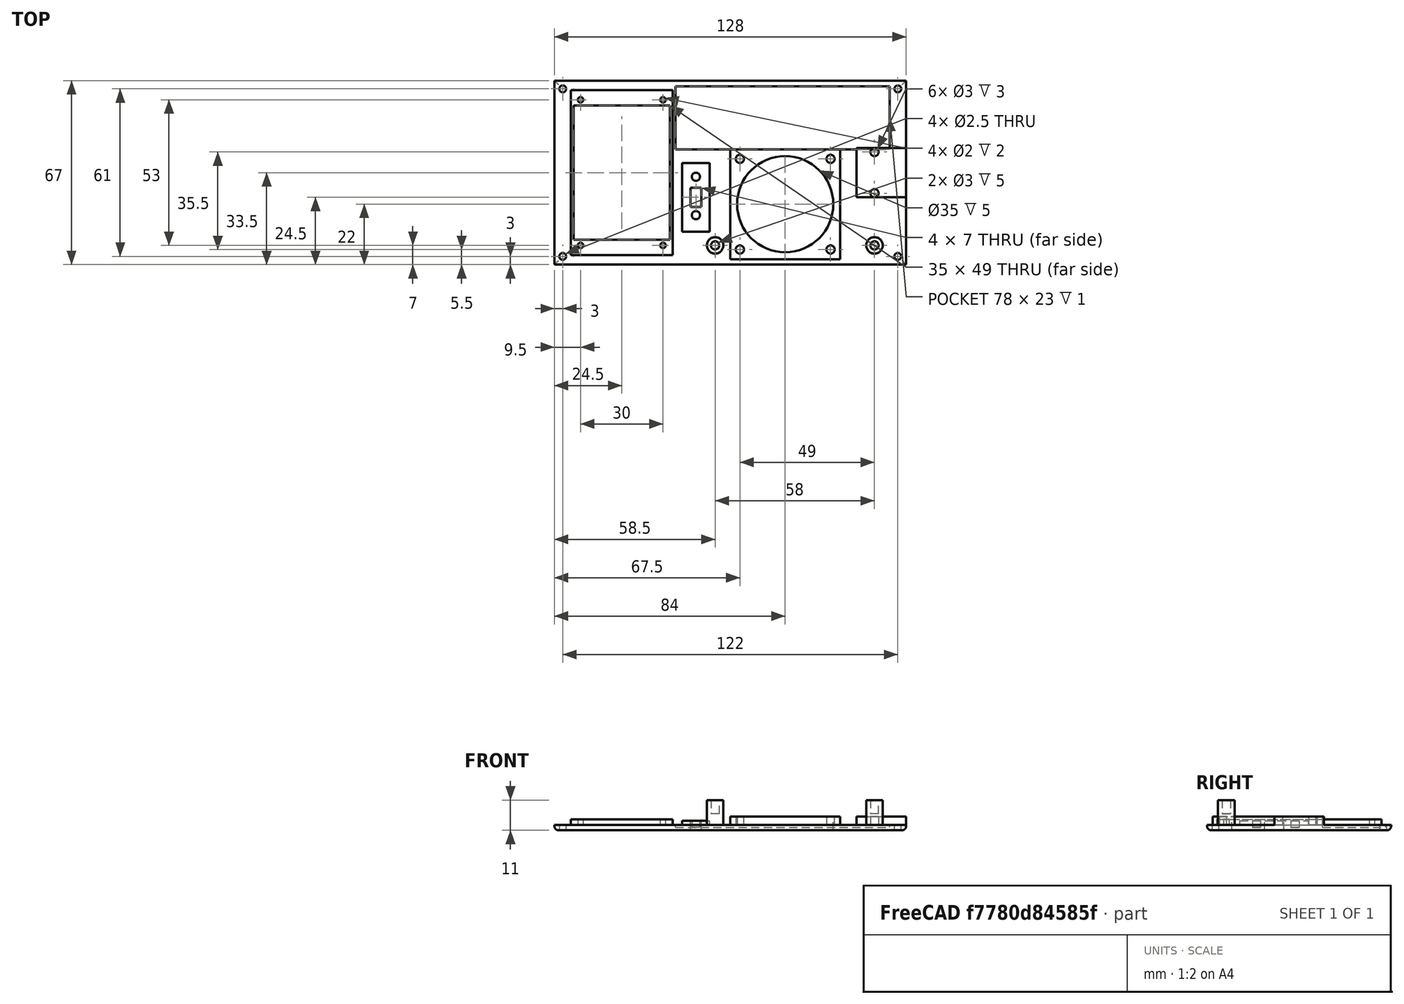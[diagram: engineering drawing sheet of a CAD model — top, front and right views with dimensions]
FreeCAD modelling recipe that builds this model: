
FCSTD DOCUMENT  (FreeCAD 1.0R39319 (Git))
Label: caseTopRedesign
License: All rights reserved
LicenseURL: https://en.wikipedia.org/wiki/All_rights_reserved
objects: PartDesign::SubtractiveCylinder×19, PartDesign::AdditiveBox×5, PartDesign::SubtractiveBox×3, PartDesign::AdditiveCylinder×2, PartDesign::Fillet×1, PartDesign::Body×1
note: 91 computed .brp shape members not serialized (recipe doc carries the construction recipe); baked Part::Feature solids carry a one-line shape summary decoded from their .brp

FEATURE [PartDesign::AdditiveBox] Box  label="base"
  AttacherType = Attacher::AttachEngine3D
  Height = 2
  Length = 128
  Refine = true
  Suppressed = false
  Width = 67
FEATURE [PartDesign::AdditiveBox] Box001  label="screenBase"
  AttacherType = Attacher::AttachEngine3D
  AttachmentOffset = pos=(6,3.5,0) rot=(0,0,1;0rad)
  AttachmentSupport = -> [Box]
  BaseFeature = -> Box
  Height = 2
  Length = 37
  MapMode = 5
  Placement = pos=(6,3.5,2) rot=(0,0,1;0rad)
  Refine = true
  Suppressed = false
  Width = 60
FEATURE [PartDesign::SubtractiveBox] Box002  label="screenCutout"
  AttacherType = Attacher::AttachEngine3D
  AttachmentOffset = pos=(1,5.5,-4) rot=(0,0,1;0rad)
  AttachmentSupport = -> [Box001]
  BaseFeature = -> Box001
  Height = 4
  Length = 35
  MapMode = 5
  Placement = pos=(7,9,0) rot=(0,0,1;0rad)
  Refine = true
  Suppressed = false
  Width = 49
FEATURE [PartDesign::SubtractiveBox] Box003  label="batteryRecess"
  AttacherType = Attacher::AttachEngine3D
  AttachmentOffset = pos=(37,33,-1) rot=(0,0,1;0rad)
  AttachmentSupport = -> [Box002]
  BaseFeature = -> Box002
  Height = 1
  Length = 78
  MapMode = 5
  Placement = pos=(44,42,1) rot=(0,0,1;0rad)
  Refine = true
  Suppressed = false
  Width = 23
FEATURE [PartDesign::AdditiveBox] Box004  label="clickwheelBase"
  AttacherType = Attacher::AttachEngine3D
  AttachmentOffset = pos=(20,-40,0) rot=(0,0,1;0rad)
  AttachmentSupport = -> [Box003]
  BaseFeature = -> Box003
  Height = 3
  Length = 40
  MapMode = 5
  Placement = pos=(64,2,2) rot=(0,0,1;0rad)
  Refine = true
  Suppressed = false
  Width = 40
FEATURE [PartDesign::SubtractiveCylinder] Cylinder  label="clickwheelCutout"
  Angle = 360
  AttacherType = Attacher::AttachEngine3D
  AttachmentOffset = pos=(20,20,-5) rot=(0,0,1;0rad)
  AttachmentSupport = -> [Box004]
  BaseFeature = -> Box004
  FirstAngle = 0
  Height = 5
  MapMode = 5
  Placement = pos=(84,22,0) rot=(0,0,1;0rad)
  Radius = 17.5
  Refine = true
  SecondAngle = 0
  Suppressed = false
FEATURE [PartDesign::SubtractiveCylinder] Cylinder001  label="clickwheelTopLeftScrew"
  Angle = 360
  AttacherType = Attacher::AttachEngine3D
  AttachmentOffset = pos=(-16.5,-16.5,-3) rot=(0,0,1;0rad)
  AttachmentSupport = -> [Cylinder]
  BaseFeature = -> Cylinder
  FirstAngle = 0
  Height = 3
  MapMode = 5
  Placement = pos=(67.5,5.5,2) rot=(0,0,1;0rad)
  Radius = 1.5
  Refine = true
  SecondAngle = 0
  Suppressed = false
FEATURE [PartDesign::SubtractiveCylinder] Cylinder002  label="clickwheelTopRightScrew"
  Angle = 360
  AttacherType = Attacher::AttachEngine3D
  AttachmentOffset = pos=(0,33,-3) rot=(0,0,1;0rad)
  AttachmentSupport = -> [Cylinder001]
  BaseFeature = -> Cylinder001
  FirstAngle = 0
  Height = 3
  MapMode = 5
  Placement = pos=(67.5,38.5,2) rot=(0,0,1;0rad)
  Radius = 1.5
  Refine = true
  SecondAngle = 0
  Suppressed = false
FEATURE [PartDesign::SubtractiveCylinder] Cylinder003  label="clickwheelBottomRightScrew"
  Angle = 360
  AttacherType = Attacher::AttachEngine3D
  AttachmentOffset = pos=(33,0,-3) rot=(0,0,1;0rad)
  AttachmentSupport = -> [Cylinder002]
  BaseFeature = -> Cylinder002
  FirstAngle = 0
  Height = 3
  MapMode = 5
  Placement = pos=(100.5,38.5,2) rot=(0,0,1;0rad)
  Radius = 1.5
  Refine = true
  SecondAngle = 0
  Suppressed = false
FEATURE [PartDesign::SubtractiveCylinder] Cylinder004  label="clickwheelBottomLeftScrew"
  Angle = 360
  AttacherType = Attacher::AttachEngine3D
  AttachmentOffset = pos=(0,-33,-3) rot=(0,0,1;0rad)
  AttachmentSupport = -> [Cylinder003]
  BaseFeature = -> Cylinder003
  FirstAngle = 0
  Height = 3
  MapMode = 5
  Placement = pos=(100.5,5.5,2) rot=(0,0,1;0rad)
  Radius = 1.5
  Refine = true
  SecondAngle = 0
  Suppressed = false
FEATURE [PartDesign::AdditiveBox] Box005  label="chargingBase"
  AttacherType = Attacher::AttachEngine3D
  AttachmentOffset = pos=(9.5,19,0) rot=(0,0,1;0rad)
  AttachmentSupport = -> [Cylinder004]
  BaseFeature = -> Cylinder004
  Height = 3
  Length = 18
  MapMode = 5
  Placement = pos=(110,24.5,2) rot=(0,0,1;0rad)
  Refine = true
  Suppressed = false
  Width = 18
FEATURE [PartDesign::SubtractiveCylinder] Cylinder005  label="chargingScrewLeft"
  Angle = 360
  AttacherType = Attacher::AttachEngine3D
  AttachmentOffset = pos=(6.5,1.5,-3) rot=(0,0,1;0rad)
  AttachmentSupport = -> [Box005]
  BaseFeature = -> Box005
  FirstAngle = 0
  Height = 3
  MapMode = 5
  Placement = pos=(116.5,26,2) rot=(0,0,1;0rad)
  Radius = 1.5
  Refine = true
  SecondAngle = 0
  Suppressed = false
FEATURE [PartDesign::SubtractiveCylinder] Cylinder006  label="chargingScrewRight"
  Angle = 360
  AttacherType = Attacher::AttachEngine3D
  AttachmentOffset = pos=(0,15,-3) rot=(0,0,1;0rad)
  AttachmentSupport = -> [Cylinder005]
  BaseFeature = -> Cylinder005
  FirstAngle = 0
  Height = 3
  MapMode = 5
  Placement = pos=(116.5,41,2) rot=(0,0,1;0rad)
  Radius = 1.5
  Refine = true
  SecondAngle = 0
  Suppressed = false
FEATURE [PartDesign::AdditiveCylinder] Cylinder007
  Angle = 360
  AttacherType = Attacher::AttachEngine3D
  AttachmentOffset = pos=(0,-34,0) rot=(0,0,1;0rad)
  AttachmentSupport = -> [Cylinder006]
  BaseFeature = -> Cylinder006
  FirstAngle = 0
  Height = 9
  MapMode = 5
  Placement = pos=(116.5,7,2) rot=(0,0,1;0rad)
  Radius = 3
  Refine = true
  SecondAngle = 0
  Suppressed = false
FEATURE [PartDesign::SubtractiveCylinder] Cylinder008
  Angle = 360
  AttacherType = Attacher::AttachEngine3D
  AttachmentOffset = pos=(0,0,-5) rot=(0,0,1;0rad)
  AttachmentSupport = -> [Cylinder007]
  BaseFeature = -> Cylinder007
  FirstAngle = 0
  Height = 5
  MapMode = 5
  Placement = pos=(116.5,7,6) rot=(0,0,1;0rad)
  Radius = 1.5
  Refine = true
  SecondAngle = 0
  Suppressed = false
FEATURE [PartDesign::AdditiveCylinder] Cylinder009
  Angle = 360
  AttacherType = Attacher::AttachEngine3D
  AttachmentOffset = pos=(-58,0,0) rot=(0,0,1;0rad)
  AttachmentSupport = -> [Cylinder008]
  BaseFeature = -> Cylinder008
  FirstAngle = 0
  Height = 9
  MapMode = 5
  Placement = pos=(58.5,7,2) rot=(0,0,1;0rad)
  Radius = 3
  Refine = true
  SecondAngle = 0
  Suppressed = false
FEATURE [PartDesign::SubtractiveCylinder] Cylinder010
  Angle = 360
  AttacherType = Attacher::AttachEngine3D
  AttachmentOffset = pos=(0,0,-5) rot=(0,0,1;0rad)
  AttachmentSupport = -> [Cylinder009]
  BaseFeature = -> Cylinder009
  FirstAngle = 0
  Height = 5
  MapMode = 5
  Placement = pos=(58.5,7,6) rot=(0,0,1;0rad)
  Radius = 1.5
  Refine = true
  SecondAngle = 0
  Suppressed = false
FEATURE [PartDesign::AdditiveBox] Box006  label="holdSwitchBase"
  AttacherType = Attacher::AttachEngine3D
  AttachmentOffset = pos=(-12,5,0) rot=(0,0,1;0rad)
  AttachmentSupport = -> [Cylinder010]
  BaseFeature = -> Cylinder010
  Height = 1.5
  Length = 10
  MapMode = 5
  Placement = pos=(46.5,12,2) rot=(0,0,1;0rad)
  Refine = true
  Suppressed = false
  Width = 25
FEATURE [PartDesign::SubtractiveBox] Box007  label="holdSwitchCutout"
  AttacherType = Attacher::AttachEngine3D
  AttachmentOffset = pos=(3,9,-5) rot=(0,0,1;0rad)
  AttachmentSupport = -> [Box006]
  BaseFeature = -> Box006
  Height = 6
  Length = 4
  MapMode = 5
  Placement = pos=(49.5,21,-1.5) rot=(0,0,1;0rad)
  Refine = true
  Suppressed = false
  Width = 7
FEATURE [PartDesign::SubtractiveCylinder] Cylinder011  label="holdSwitchLeftScrew"
  Angle = 360
  AttacherType = Attacher::AttachEngine3D
  AttachmentOffset = pos=(2,-3,-2.5) rot=(0,0,1;0rad)
  AttachmentSupport = -> [Box007]
  BaseFeature = -> Box007
  FirstAngle = 0
  Height = 2.5
  MapMode = 5
  Placement = pos=(51.5,18,1) rot=(0,0,1;0rad)
  Radius = 1.5
  Refine = true
  SecondAngle = 0
  Suppressed = false
FEATURE [PartDesign::SubtractiveCylinder] Cylinder012  label="holdSwitchRightScrew"
  Angle = 360
  AttacherType = Attacher::AttachEngine3D
  AttachmentOffset = pos=(0,14,-2.5) rot=(0,0,1;0rad)
  AttachmentSupport = -> [Cylinder011]
  BaseFeature = -> Cylinder011
  FirstAngle = 0
  Height = 2.5
  MapMode = 5
  Placement = pos=(51.5,32,1) rot=(0,0,1;0rad)
  Radius = 1.5
  Refine = true
  SecondAngle = 0
  Suppressed = false
FEATURE [PartDesign::SubtractiveCylinder] Cylinder013  label="screenScrewTopLeft"
  Angle = 360
  AttacherType = Attacher::AttachEngine3D
  AttachmentOffset = pos=(-42,-25,-2) rot=(0,0,1;0rad)
  AttachmentSupport = -> [Cylinder012]
  BaseFeature = -> Cylinder012
  FirstAngle = 0
  Height = 2
  MapMode = 5
  Placement = pos=(9.5,7,2) rot=(0,0,1;0rad)
  Radius = 1
  Refine = true
  SecondAngle = 0
  Suppressed = false
FEATURE [PartDesign::SubtractiveCylinder] Cylinder014  label="screenScrewTopRight"
  Angle = 360
  AttacherType = Attacher::AttachEngine3D
  AttachmentOffset = pos=(0,53,-2) rot=(0,0,1;0rad)
  AttachmentSupport = -> [Cylinder013]
  BaseFeature = -> Cylinder013
  FirstAngle = 0
  Height = 2
  MapMode = 5
  Placement = pos=(9.5,60,2) rot=(0,0,1;0rad)
  Radius = 1
  Refine = true
  SecondAngle = 0
  Suppressed = false
FEATURE [PartDesign::SubtractiveCylinder] Cylinder015  label="screenScrewBottomRight"
  Angle = 360
  AttacherType = Attacher::AttachEngine3D
  AttachmentOffset = pos=(30,0,-2) rot=(0,0,1;0rad)
  AttachmentSupport = -> [Cylinder014]
  BaseFeature = -> Cylinder014
  FirstAngle = 0
  Height = 2
  MapMode = 5
  Placement = pos=(39.5,60,2) rot=(0,0,1;0rad)
  Radius = 1
  Refine = true
  SecondAngle = 0
  Suppressed = false
FEATURE [PartDesign::SubtractiveCylinder] Cylinder016  label="screenScrewBottomLeft"
  Angle = 360
  AttacherType = Attacher::AttachEngine3D
  AttachmentOffset = pos=(0,-53,-2) rot=(0,0,1;0rad)
  AttachmentSupport = -> [Cylinder015]
  BaseFeature = -> Cylinder015
  FirstAngle = 0
  Height = 2
  MapMode = 5
  Placement = pos=(39.5,7,2) rot=(0,0,1;0rad)
  Radius = 1
  Refine = true
  SecondAngle = 0
  Suppressed = false
FEATURE [PartDesign::SubtractiveCylinder] Cylinder017  label="topLeftScrew"
  Angle = 360
  AttacherType = Attacher::AttachEngine3D
  AttachmentOffset = pos=(-36.5,-4,-2) rot=(0,0,1;0rad)
  AttachmentSupport = -> [Cylinder016]
  BaseFeature = -> Cylinder016
  FirstAngle = 0
  Height = 2
  MapMode = 5
  Placement = pos=(3,3,0) rot=(0,0,1;0rad)
  Radius = 1.25
  Refine = true
  SecondAngle = 0
  Suppressed = false
FEATURE [PartDesign::SubtractiveCylinder] Cylinder018  label="topRightScrew"
  Angle = 360
  AttacherType = Attacher::AttachEngine3D
  AttachmentOffset = pos=(0,61,-2) rot=(0,0,1;0rad)
  AttachmentSupport = -> [Cylinder017]
  BaseFeature = -> Cylinder017
  FirstAngle = 0
  Height = 2
  MapMode = 5
  Placement = pos=(3,64,0) rot=(0,0,1;0rad)
  Radius = 1.25
  Refine = true
  SecondAngle = 0
  Suppressed = false
FEATURE [PartDesign::SubtractiveCylinder] Cylinder019  label="bottomRightScrew"
  Angle = 360
  AttacherType = Attacher::AttachEngine3D
  AttachmentOffset = pos=(122,0,-2) rot=(0,0,1;0rad)
  AttachmentSupport = -> [Cylinder018]
  BaseFeature = -> Cylinder018
  FirstAngle = 0
  Height = 2
  MapMode = 5
  Placement = pos=(125,64,0) rot=(0,0,1;0rad)
  Radius = 1.25
  Refine = true
  SecondAngle = 0
  Suppressed = false
FEATURE [PartDesign::SubtractiveCylinder] Cylinder020  label="bottomLeftScrew"
  Angle = 360
  AttacherType = Attacher::AttachEngine3D
  AttachmentOffset = pos=(0,-61,-2) rot=(0,0,1;0rad)
  AttachmentSupport = -> [Cylinder019]
  BaseFeature = -> Cylinder019
  FirstAngle = 0
  Height = 2
  MapMode = 5
  Placement = pos=(125,3,0) rot=(0,0,1;0rad)
  Radius = 1.25
  Refine = true
  SecondAngle = 0
  Suppressed = false
FEATURE [PartDesign::Fillet] Fillet
  Base = -> Cylinder020 [Edge5,Edge4,Edge37,Edge39]
  BaseFeature = -> Cylinder020
  Placement = pos=(125,3,0) rot=(0,0,1;0rad)
  Radius = 1.5
  Refine = true
  SupportTransform = false
  Suppressed = false
  UseAllEdges = false
FEATURE [PartDesign::Body] Body
  AllowCompound = false
  Group = -> [Box,Box001,Box002,Box003,Box004,Cylinder,Cylinder001,Cylinder002,Cylinder003,Cylinder004,Box005,Cylinder005,Cylinder006,Cylinder007,Cylinder008,Cylinder009,Cylinder010,Box006,Box007,Cylinder011,Cylinder012,Cylinder013,Cylinder014,Cylinder015,Cylinder016,Cylinder017,Cylinder018,Cylinder019,Cylinder020,Fillet]
  Origin = -> Origin
  Tip = -> Fillet
